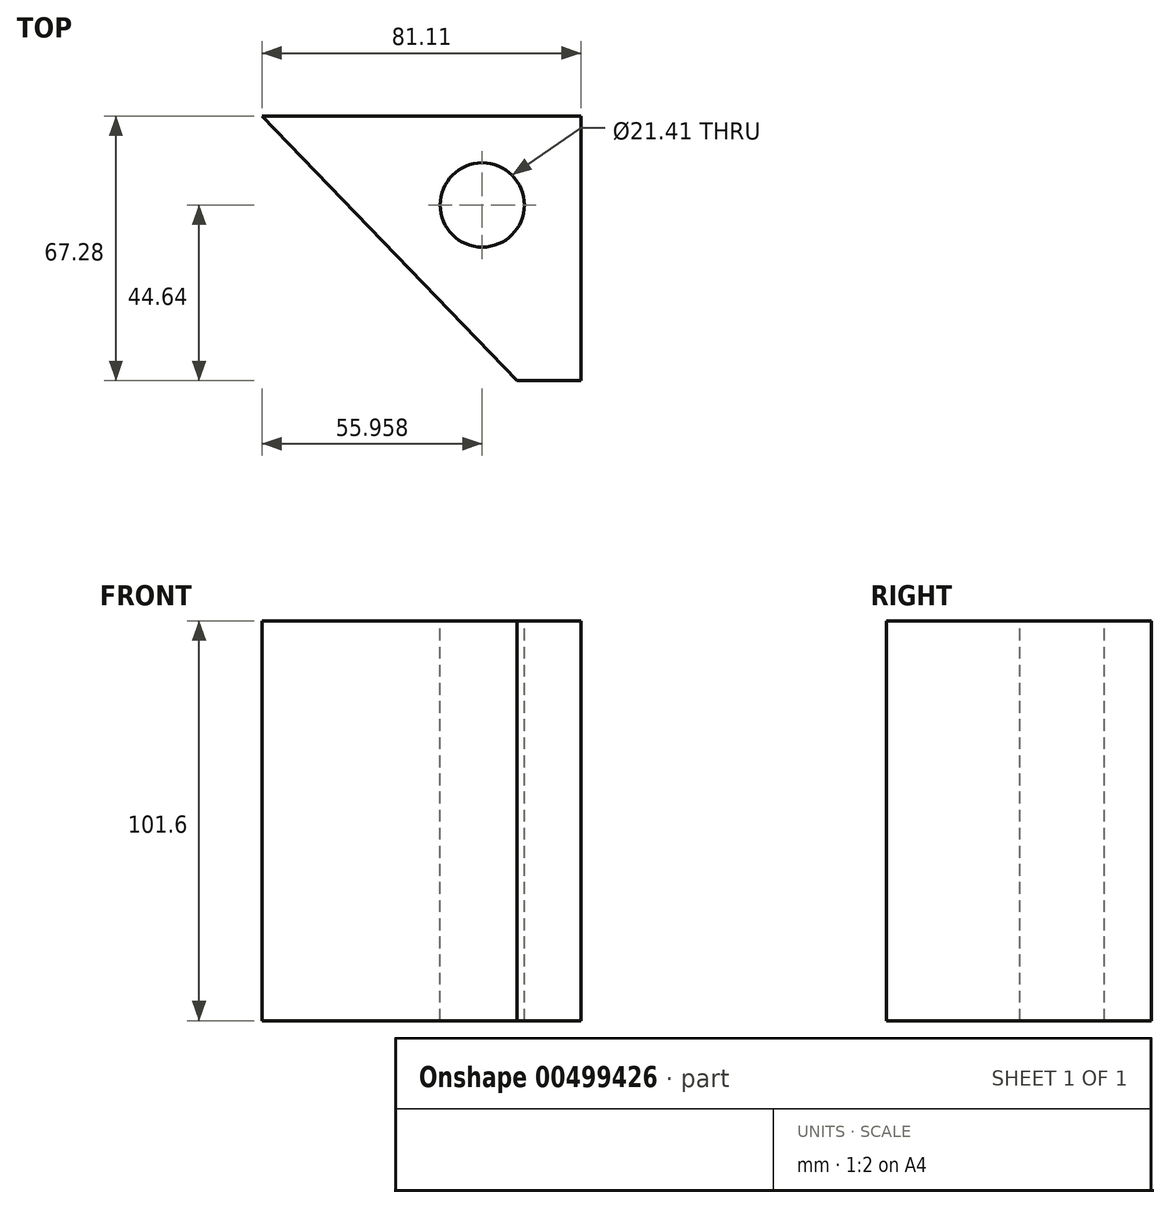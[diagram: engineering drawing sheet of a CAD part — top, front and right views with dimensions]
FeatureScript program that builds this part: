
annotation { "Feature Type Name" : "Feature", "Feature Type Description" : "" }
export const myFeature = defineFeature(function(context is Context, id is Id, definition is map)
    precondition{}
    {
        {
            var Q0;
            Q0=qCreatedBy(makeId("Top.planeOp"),FACE);
            var sketch = newSketch(context, id + "F0", { "sketchPlane" : qUnion([Q0])});
            skLineSegment(sketch, "E0.right", {"start": v(51.56, 31.6) * mm, "end": v(51.56, -35.68) * mm});
            skLineSegment(sketch, "E1", {"start": v(-29.55, 31.6) * mm, "end": v(35.21, -35.68) * mm});
            skLineSegment(sketch, "E2", {"start": v(-29.55, 31.6) * mm, "end": v(51.56, 31.6) * mm});
            skLineSegment(sketch, "E3", {"start": v(51.56, -35.68) * mm, "end": v(35.21, -35.68) * mm});
            skSolve(sketch);
        }
        {
            var Q0;
            Q0=makeQuery(id+"F0.imprint","IMPRINT",FACE,{"disambiguationData":[TD([[makeQuery(id+"F0.imprint","IMPRINT",EDGE,{"derivedFrom":sQuery(id+"F0.wireOp",EDGE,"E0.right")}),-1.0]])]});
            extrude(context, id + "F1", {"entities" : qUnion([Q0]), "depth" : 101.6 * mm});
        }
        {
            var Q0;
            Q0=makeQuery(id+"F1.opExtrude","CAP_FACE",FACE,{"disambiguationData":[OSD([sQuery(id+"F0.wireOp",EDGE,"E0.right"),sQuery(id+"F0.wireOp",EDGE,"E1"),sQuery(id+"F0.wireOp",EDGE,"E2"),sQuery(id+"F0.wireOp",EDGE,"E3")])],"isStart":false});
            var sketch = newSketch(context, id + "F2", { "sketchPlane" : qUnion([Q0])});
            skCircle(sketch, "E4", {"center": v(26.4, 8.96) * mm, "radius": 10.7 * mm});
            skSolve(sketch);
        }
        {
            var Q0;
            Q0=makeQuery(id+"F2.imprint","IMPRINT",FACE,{"disambiguationData":[TD([[makeQuery(id+"F2.imprint","IMPRINT",EDGE,{"derivedFrom":sQuery(id+"F2.wireOp",EDGE,"E4")}),1.0]])]});
            extrude(context, id + "F3", {"entities" : qUnion([Q0]), "operationType" : NewBodyOperationType.REMOVE, "oppositeDirection" : true, "depth" : 101.6 * mm});
        }
    });
